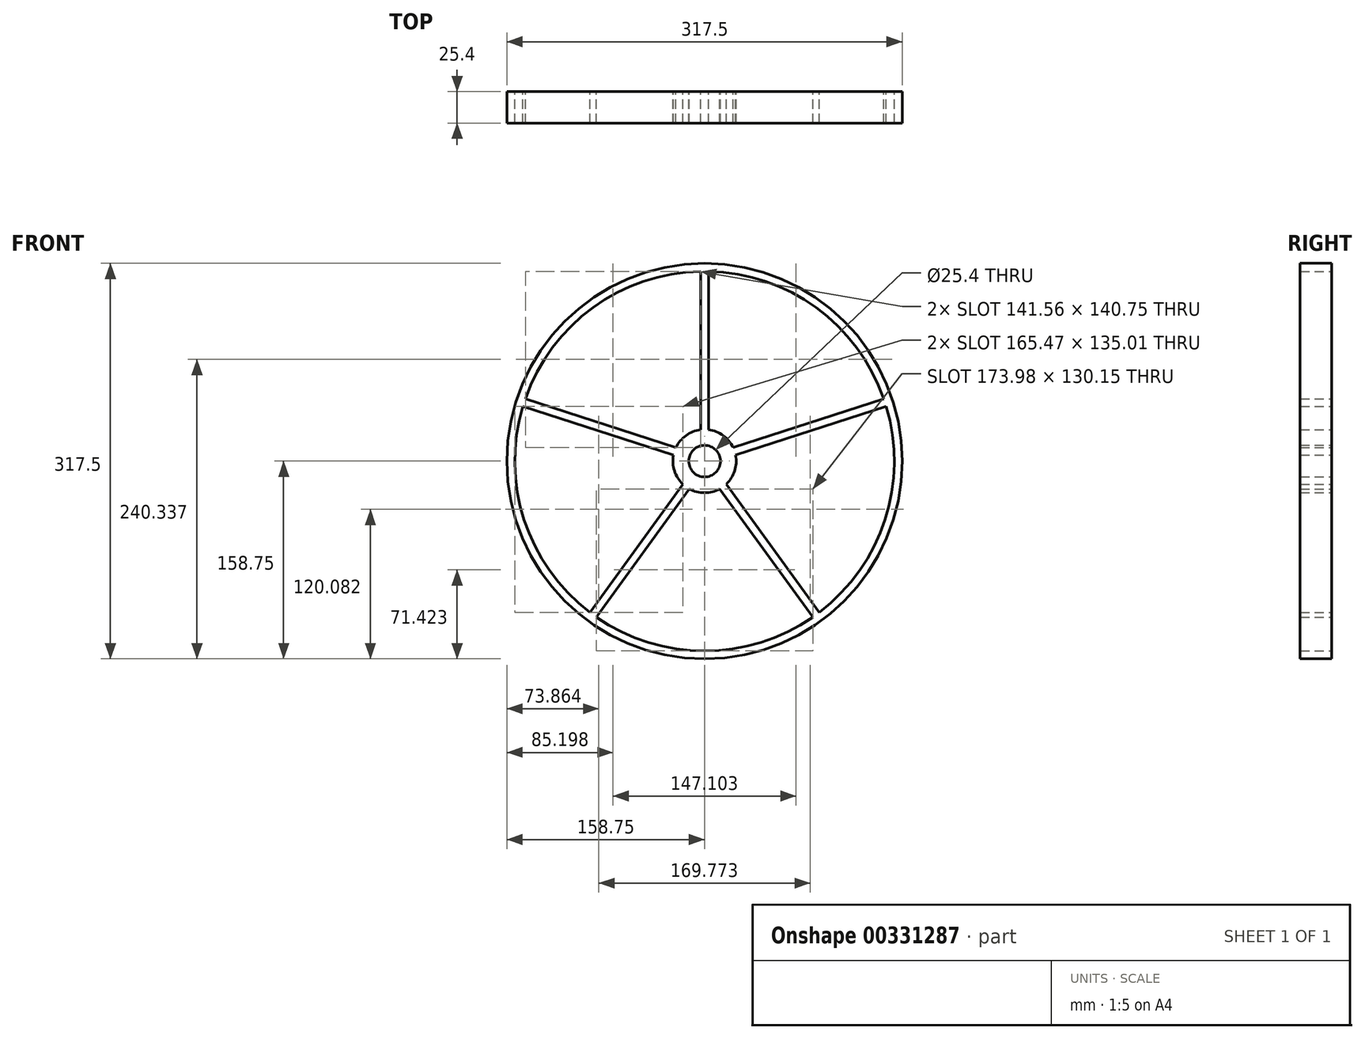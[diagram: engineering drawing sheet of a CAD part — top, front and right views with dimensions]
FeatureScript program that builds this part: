
annotation { "Feature Type Name" : "Feature", "Feature Type Description" : "" }
export const myFeature = defineFeature(function(context is Context, id is Id, definition is map)
    precondition{}
    {
        {
            var Q0;
            Q0=qCreatedBy(makeId("Front.planeOp"),FACE);
            var sketch = newSketch(context, id + "F0", { "sketchPlane" : qUnion([Q0])});
            skCircle(sketch, "E0", {"center": v(0, 0) * mm, "radius": 12.7 * mm});
            skArc(sketch, "E1", {"start": v(-3.18, 152.37) * mm, "mid": v(-89.58, 123.3) * mm, "end": v(-143.93, 50.1) * mm});
            skCircle(sketch, "E2.0", {"center": v(0, 0) * mm, "radius": 158.75 * mm});
            skArc(sketch, "E3.0", {"start": v(-3.18, 25.2) * mm, "mid": v(-14.93, 20.55) * mm, "end": v(-22.99, 10.8) * mm});
            skLineSegment(sketch, "E4", {"start": v(0, 25.4) * mm, "end": v(0, 152.4) * mm});
            skLineSegment(sketch, "E5.0", {"start": v(3.17, 25.2) * mm, "end": v(3.17, 152.37) * mm});
            skLineSegment(sketch, "E6.MirrorCS", {"start": v(-3.17, 25.2) * mm, "end": v(-3.17, 152.37) * mm});
            skLineSegment(sketch, "E7.1.0", {"start": v(22.99, 10.8) * mm, "end": v(143.93, 50.1) * mm});
            skLineSegment(sketch, "E7.1.1", {"start": v(24.95, 4.77) * mm, "end": v(145.9, 44.06) * mm});
            skLineSegment(sketch, "E7.2.0", {"start": v(17.38, -18.52) * mm, "end": v(92.13, -121.4) * mm});
            skLineSegment(sketch, "E7.2.1", {"start": v(12.24, -22.25) * mm, "end": v(87, -125.13) * mm});
            skLineSegment(sketch, "E7.3.0", {"start": v(-12.24, -22.25) * mm, "end": v(-87, -125.13) * mm});
            skLineSegment(sketch, "E7.3.1", {"start": v(-17.38, -18.52) * mm, "end": v(-92.13, -121.4) * mm});
            skLineSegment(sketch, "E7.4.0", {"start": v(-24.95, 4.77) * mm, "end": v(-145.9, 44.06) * mm});
            skLineSegment(sketch, "E7.4.1", {"start": v(-22.99, 10.8) * mm, "end": v(-143.93, 50.1) * mm});
            skLineSegment(sketch, "E7.anchor1", {"start": v(0, 0) * mm, "end": v(-3.17, 25.2) * mm, "construction": true});
            skLineSegment(sketch, "E7.anchor2", {"start": v(0, 0) * mm, "end": v(-24.95, 4.77) * mm, "construction": true});
            skArc(sketch, "E8.trimOffspring", {"start": v(-24.95, 4.77) * mm, "mid": v(-24.16, -7.85) * mm, "end": v(-17.38, -18.52) * mm});
            skArc(sketch, "E9.trimOffspring", {"start": v(22.99, 10.8) * mm, "mid": v(14.93, 20.55) * mm, "end": v(3.17, 25.2) * mm});
            skArc(sketch, "E10.trimOffspring", {"start": v(17.38, -18.52) * mm, "mid": v(24.16, -7.85) * mm, "end": v(24.95, 4.77) * mm});
            skArc(sketch, "E11.trimOffspring", {"start": v(-12.24, -22.25) * mm, "mid": v(0, -25.4) * mm, "end": v(12.24, -22.25) * mm});
            skArc(sketch, "E12.trimOffspring", {"start": v(143.93, 50.1) * mm, "mid": v(89.58, 123.3) * mm, "end": v(3.18, 152.37) * mm});
            skArc(sketch, "E13.trimOffspring", {"start": v(92.13, -121.4) * mm, "mid": v(144.94, -47.1) * mm, "end": v(145.9, 44.06) * mm});
            skArc(sketch, "E14.trimOffspring", {"start": v(-87, -125.13) * mm, "mid": v(0, -152.4) * mm, "end": v(87, -125.13) * mm});
            skArc(sketch, "E15.trimOffspring", {"start": v(-145.9, 44.06) * mm, "mid": v(-144.94, -47.1) * mm, "end": v(-92.13, -121.4) * mm});
            skSolve(sketch);
        }
        {
            var Q0;
            Q0=makeQuery(id+"F0.imprint","IMPRINT",FACE,{"disambiguationData":[TD([[makeQuery(id+"F0.imprint","IMPRINT",EDGE,{"derivedFrom":sQuery(id+"F0.wireOp",EDGE,"E0")}),-1.0]])]});
            extrude(context, id + "F1", {"entities" : qUnion([Q0]), "depth" : 25.4 * mm, "offsetDistance" : 25.4 * mm});
        }
    });
